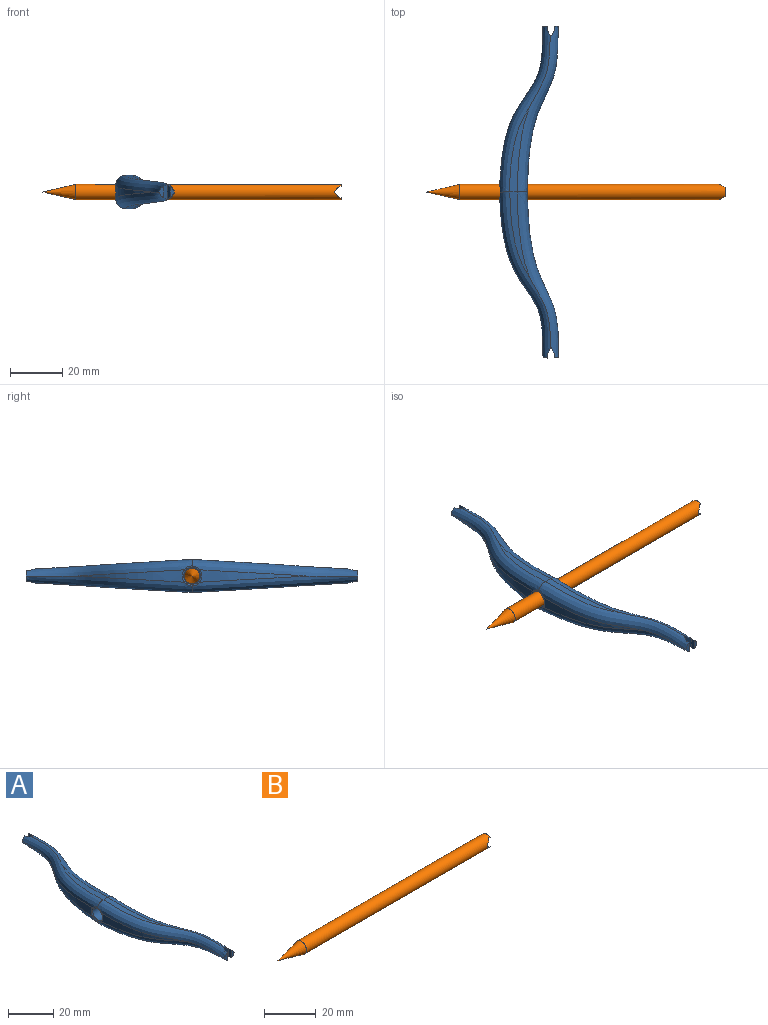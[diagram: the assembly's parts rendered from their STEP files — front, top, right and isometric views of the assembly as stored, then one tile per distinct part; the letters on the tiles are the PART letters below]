
ASSEMBLY  parts=2 mates=1
PART A: 35 faces, bbox 22.9x135.9x13.2 mm
  f0: extruded ~41x14.1mm, area 102.6mm2, adj f24,f25,f32
  f1: extruded ~38.6x8.76mm, area 94.2mm2, adj f16,f27,f28
  f2: extruded ~40.9x14.09mm, area 102.7mm2, adj f21,f22,f31
  f3: plane 4.2x1.82mm, normal (0,-1,0), area 4.8mm2, adj f4,f21,f22
  f4: plane 4.38x1.59mm, normal (1,0,0), area 6.8mm2, adj f3,f5,f21,f22
  f5: plane 5.38x2.54mm, normal (0.89,-0.45,0), area 14.2mm2, adj f4,f6,f21,f22,f23,f26
  f6: plane 5.33x2.55mm, normal (-0.89,-0.45,0), area 13.4mm2, adj f5,f7,f23,f26
  f7: plane 3.97x1.59mm, normal (-1,0,0), area 6.2mm2, adj f6,f8,f23,f26
  f8: plane 3.91x1.58mm, normal (0,-1,0), area 3.7mm2, adj f7,f23,f26
  f9: extruded ~38.62x8.82mm, area 94.2mm2, adj f16,f23,f26
  f10: plane 3.9x1.56mm, normal (0,1,0), area 3.7mm2, adj f11,f27,f28
  f11: plane 4.07x1.59mm, normal (-1,0,0), area 6.3mm2, adj f10,f12,f27,f28
  f12: plane 5.4x2.54mm, normal (-0.89,0.45,0), area 13.7mm2, adj f11,f13,f27,f28
  f13: plane 5.44x2.55mm, normal (0.89,0.45,0), area 14.3mm2, adj f12,f14,f24,f25,f27,f28
  f14: plane 4.39x1.59mm, normal (1,0,0), area 6.8mm2, adj f13,f15,f24,f25
  f15: plane 4.23x1.85mm, normal (0,1,0), area 4.8mm2, adj f14,f24,f25
  f16: cylinder r=3.17mm len=10.02mm, axis (1,0,0), area 198mm2, adj f1,f9,f23,f26,f27,f28,f29,f30
  f17: plane 32.18x7.44mm, normal (0,-0.06,-1), area 70.1mm2, adj f18,f22,f26,f28
  f18: plane 32.65x7.59mm, normal (0,0.06,-1), area 70.4mm2, adj f17,f22,f25,f28
  f19: plane 32.19x7.44mm, normal (0,-0.06,1), area 70.1mm2, adj f20,f21,f23,f27
  f20: plane 32.65x7.59mm, normal (0,0.06,1), area 70.4mm2, adj f19,f21,f24,f27
  f21: bspline ~67.26x20.16mm, area 355.8mm2, adj f2,f3,f4,f5,f19,f20,f22,f23
  f22: bspline ~71.19x20.17mm, area 355.7mm2, adj f2,f3,f4,f5,f17,f18,f21,f25
  f23: bspline ~66.68x16.02mm, area 351.8mm2, adj f5,f6,f7,f8,f9,f16,f19,f21
  f24: bspline ~68.97x20.15mm, area 367.5mm2, adj f0,f13,f14,f15,f20,f21,f25,f27
  f25: bspline ~67.28x20.14mm, area 367.5mm2, adj f0,f13,f14,f15,f18,f22,f24,f28
  f26: bspline ~70.59x16.12mm, area 351.8mm2, adj f5,f6,f7,f8,f9,f16,f17,f22
  f27: bspline ~69.03x15.97mm, area 353.4mm2, adj f1,f10,f11,f12,f13,f16,f19,f20
  f28: bspline ~68.49x15.99mm, area 353.4mm2, adj f1,f10,f11,f12,f13,f16,f17,f18
  f29: bspline ~3.56x2.23mm, area 2.7mm2, adj f16,f21,f30,f31
  f30: bspline ~3.57x2.23mm, area 2.7mm2, adj f16,f24,f29,f32
  f31: bspline ~5.88x1.79mm, area 3.8mm2, adj f2,f16,f29,f33
  f32: bspline ~5.47x1.79mm, area 3.8mm2, adj f0,f16,f30,f34
  f33: bspline ~3.56x2.23mm, area 2.7mm2, adj f16,f22,f31,f34
  f34: bspline ~3.57x2.23mm, area 2.7mm2, adj f16,f25,f32,f33
PART B: 10 faces, bbox 114.3x5.8x5.8 mm
  f0: plane 3.64x0.64mm, normal (1,0,0), area 1.6mm2, adj f1,f4
  f1: cylinder r=2.92mm len=101.6mm, axis (-1,0,0), area 1847.3mm2, adj f0,f2,f3,f4,f5,f6,f7,f8
  f2: plane 3.64x0.64mm, normal (1,0,0), area 1.6mm2, adj f1,f5
  f3: cone r=2.92mm half-angle=13deg, axis (1,0,0), area 119.6mm2, adj f1
  f4: plane 3.64x0.64mm, normal (0,0,1), area 2.3mm2, adj f0,f1,f6
  f5: plane 3.64x0.64mm, normal (0,0,-1), area 2.3mm2, adj f1,f2,f7
  f6: plane 5.64x1.53mm, normal (0.71,0,0.71), area 10.6mm2, adj f1,f4,f9
  f7: plane 5.64x1.53mm, normal (0.71,0,-0.71), area 10.6mm2, adj f1,f5,f8
  f8: cylinder r=1.27mm len=5.84mm, axis (0,1,0), area 4.9mm2, adj f1,f7,f9
  f9: cylinder r=1.27mm len=5.84mm, axis (0,1,0), area 4.9mm2, adj f1,f6,f8
PLACE A rot(axis=(1,0,0),180deg) t=(4.46,-1.38,8.77)mm
PLACE B rot(axis=(1,0,0),180deg) t=(44.76,25.42,2.42)mm
MATE slider B.f1 <-> A.f16  axis (-1,0,0) through (-1.57,0.25,2.42)mm
